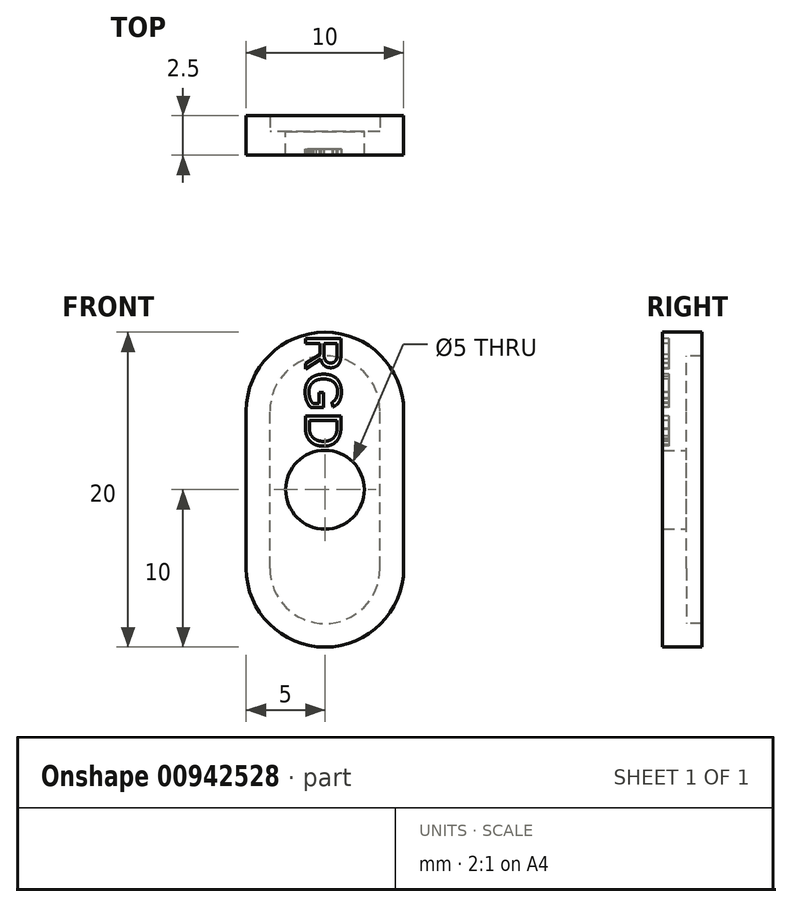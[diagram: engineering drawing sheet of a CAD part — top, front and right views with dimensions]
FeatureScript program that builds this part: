
annotation { "Feature Type Name" : "Feature", "Feature Type Description" : "" }
export const myFeature = defineFeature(function(context is Context, id is Id, definition is map)
    precondition{}
    {
        {
            var Q0;
            Q0=qCreatedBy(makeId("Front.planeOp"),FACE);
            var sketch = newSketch(context, id + "F0", { "sketchPlane" : qUnion([Q0])});
            skLineSegment(sketch, "E0.bottom", {"start": v(0, -10) * mm, "end": v(0, -10) * mm});
            skLineSegment(sketch, "E0.top", {"start": v(0, 10) * mm, "end": v(0, 10) * mm});
            skLineSegment(sketch, "E0.left", {"start": v(5, -5) * mm, "end": v(5, 5) * mm});
            skLineSegment(sketch, "E0.right", {"start": v(-5, -5) * mm, "end": v(-5, 5) * mm});
            skPoint(sketch, "E0.middle", {"position": v(0, 0) * mm});
            skPoint(sketch, "E1.visualSharp", {"position": v(-5, 10) * mm});
            skArc(sketch, "E1.filletArc", {"start": v(0, 10) * mm, "mid": v(-3.54, 8.54) * mm, "end": v(-5, 5) * mm});
            skPoint(sketch, "E2.visualSharp", {"position": v(5, 10) * mm});
            skArc(sketch, "E2.filletArc", {"start": v(5, 5) * mm, "mid": v(3.54, 8.54) * mm, "end": v(0, 10) * mm});
            skPoint(sketch, "E3.visualSharp", {"position": v(5, -10) * mm});
            skArc(sketch, "E3.filletArc", {"start": v(0, -10) * mm, "mid": v(3.54, -8.54) * mm, "end": v(5, -5) * mm});
            skPoint(sketch, "E4.visualSharp", {"position": v(-5, -10) * mm});
            skArc(sketch, "E4.filletArc", {"start": v(-5, -5) * mm, "mid": v(-3.54, -8.54) * mm, "end": v(0, -10) * mm});
            skLineSegment(sketch, "E5.0", {"start": v(3.5, -5) * mm, "end": v(3.5, 5) * mm});
            skArc(sketch, "E5.1", {"start": v(0, 8.5) * mm, "mid": v(-2.47, 7.47) * mm, "end": v(-3.5, 5) * mm});
            skLineSegment(sketch, "E5.2", {"start": v(-3.5, -5) * mm, "end": v(-3.5, 5) * mm});
            skArc(sketch, "E5.3", {"start": v(3.5, 5) * mm, "mid": v(2.47, 7.47) * mm, "end": v(0, 8.5) * mm});
            skArc(sketch, "E5.4", {"start": v(-3.5, -5) * mm, "mid": v(-2.47, -7.47) * mm, "end": v(0, -8.5) * mm});
            skArc(sketch, "E5.5", {"start": v(0, -8.5) * mm, "mid": v(2.47, -7.47) * mm, "end": v(3.5, -5) * mm});
            skCircle(sketch, "E6", {"center": v(0, 0) * mm, "radius": 2.5 * mm});
            skSolve(sketch);
        }
        {
            var Q0;
            Q0=makeQuery(id+"F0.imprint","IMPRINT",FACE,{"disambiguationData":[TD([[makeQuery(id+"F0.imprint","IMPRINT",EDGE,{"derivedFrom":sQuery(id+"F0.wireOp",EDGE,"E0.left")}),1.0]])]});
            var Q1;
            Q1=makeQuery(id+"F0.imprint","IMPRINT",FACE,{"disambiguationData":[TD([[makeQuery(id+"F0.imprint","IMPRINT",EDGE,{"derivedFrom":sQuery(id+"F0.wireOp",EDGE,"E5.0")}),1.0]])]});
            extrude(context, id + "F1", {"entities" : qUnion([Q0, Q1]), "depth" : 1.5 * mm, "offsetDistance" : 25 * mm});
        }
        {
            var Q0;
            Q0=makeQuery(id+"F0.imprint","IMPRINT",FACE,{"disambiguationData":[TD([[makeQuery(id+"F0.imprint","IMPRINT",EDGE,{"derivedFrom":sQuery(id+"F0.wireOp",EDGE,"E0.left")}),1.0]])]});
            extrude(context, id + "F2", {"entities" : qUnion([Q0]), "operationType" : NewBodyOperationType.ADD, "oppositeDirection" : true, "depth" : 1 * mm, "offsetDistance" : 25 * mm});
        }
        {
            var Q0;
            Q0=makeQuery(id+"F1.opExtrude","CAP_FACE",FACE,{"disambiguationData":[OSD([sQuery(id+"F0.wireOp",EDGE,"E0.left"),sQuery(id+"F0.wireOp",EDGE,"E0.right"),sQuery(id+"F0.wireOp",EDGE,"E1.filletArc"),sQuery(id+"F0.wireOp",EDGE,"E2.filletArc"),sQuery(id+"F0.wireOp",EDGE,"E3.filletArc"),sQuery(id+"F0.wireOp",EDGE,"E4.filletArc"),sQuery(id+"F0.wireOp",EDGE,"E6")])],"isStart":false});
            var sketch = newSketch(context, id + "F3", { "sketchPlane" : qUnion([Q0])});
            skText(sketch, "E7", { "text": "RGD", "fontName": "Arimo-Regular.ttf"});
            const initialGuessF3  = {"E7": [-0.00123, 0.00986, 0, -1, 0.00235]};
            skSetInitialGuess(sketch, initialGuessF3);
            skSolve(sketch);
        }
        {
            var Q0;
            Q0 = qSketchRegion(id + "F3", true);
            extrude(context, id + "F4", {"entities" : qUnion([Q0]), "operationType" : NewBodyOperationType.REMOVE, "oppositeDirection" : true, "depth" : .4 * mm, "offsetDistance" : 25 * mm});
        }
    });
